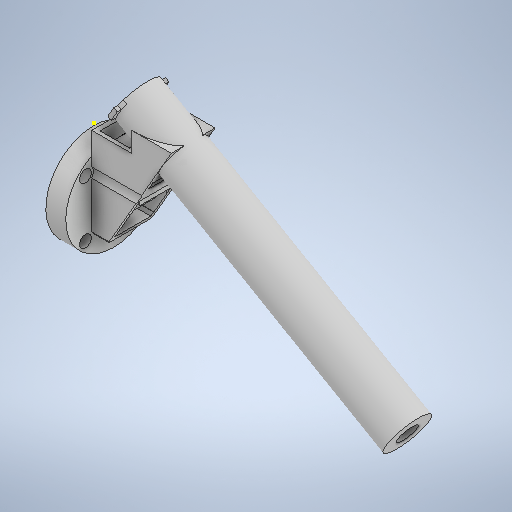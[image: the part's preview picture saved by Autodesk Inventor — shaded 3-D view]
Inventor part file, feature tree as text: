
AUTODESK INVENTOR PART (.ipt)
format: ipt  version: 2025.1 (Build 291241000, 241)  size: 426,496 bytes
history: native  units: mm
features: sketch x7, extrude x6, other x4
ambient origin geometry x8: Origin, YZ Plane, XZ Plane, XY Plane, X Axis, Y Axis, Z Axis, Center Point
bodies: Body1 (feature_tree)
feature tree (17):
  other  "Soporte marcador robotica r3 (1).ipt"
  extrude  "Extrusión1"  Depth=8.0mm
  extrude  "Extrusión2"  Depth=8.0mm
  extrude  "Extrusión3"  Depth=25.0mm TaperAngle=0.0deg
  extrude  "Extrusión4"  Depth=8.0mm TaperAngle=0.0deg
  sketch  "Boceto5"  dims[d11=8.0mm d12=0.0mm d13=12.0mm d14=0.0mm]
  extrude  "Extrusión5"  Depth=12.0mm TaperAngle=0.0deg
  extrude  "Extrusión6"  [1 undecoded]
  other  "Sólido1::Soporte marcador robotica r3 (1).ipt"
  other  "OperaciónIdentificador1"
  sketch  "Boceto1"  dims[d0=10.0mm d1=8.0mm]
  sketch  "Boceto2"  dims[d2=8.0mm d3=8.0mm]
  sketch  "Boceto3"  dims[d4=8.0mm d5=25.0mm d6=0.0mm]
  sketch  "Boceto4"  dims[d7=25.0mm d8=0.0mm d9=8.0mm d10=0.0mm]
  sketch  "Boceto6"  dims[d15=12.0mm d16=0.0mm]
  sketch  "Boceto7"
  other  "Sólido1"
note: 1 required parameter value undecoded (feature->parameter linkage not recoverable at this tier; creation-order binding heuristic only, values carry confidence <= 0.55)
